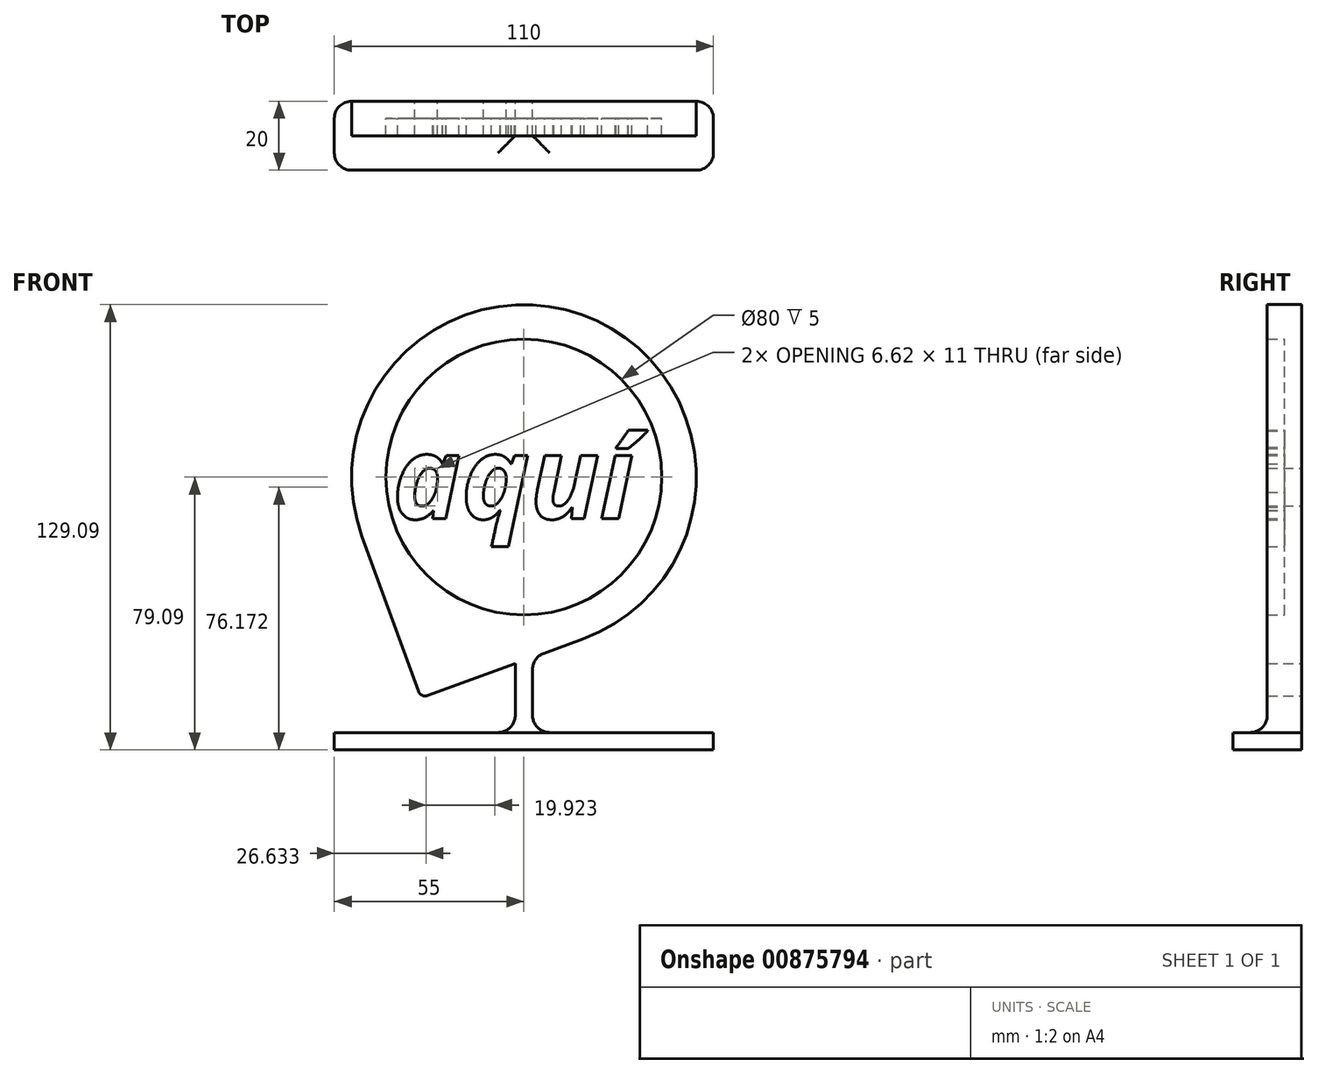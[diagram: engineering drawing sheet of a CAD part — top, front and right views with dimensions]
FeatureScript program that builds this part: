
annotation { "Feature Type Name" : "Feature", "Feature Type Description" : "" }
export const myFeature = defineFeature(function(context is Context, id is Id, definition is map)
    precondition{}
    {
        {
            var Q0;
            Q0=qCreatedBy(makeId("Front.planeOp"),FACE);
            var sketch = newSketch(context, id + "F0", { "sketchPlane" : qUnion([Q0])});
            skCircle(sketch, "E0", {"center": v(0, 0) * mm, "radius": 40 * mm});
            skText(sketch, "E1", { "text": "aquí", "fontName": "OpenSans-BoldItalic.ttf"});
            skArc(sketch, "E2", {"start": v(17.1, -46.98) * mm, "mid": v(21.13, 45.32) * mm, "end": v(-46.98, -17.1) * mm});
            skLineSegment(sketch, "E3", {"start": v(-46.98, -17.1) * mm, "end": v(-29.88, -64.09) * mm});
            skLineSegment(sketch, "E4", {"start": v(-29.88, -64.09) * mm, "end": v(17.1, -46.98) * mm});
            skLineSegment(sketch, "E5", {"start": v(0, 0) * mm, "end": v(0, -76.59) * mm, "construction": true});
            skLineSegment(sketch, "E6.bottom", {"start": v(55, -74.09) * mm, "end": v(-55, -74.09) * mm});
            skLineSegment(sketch, "E6.top", {"start": v(55, -79.09) * mm, "end": v(-55, -79.09) * mm});
            skLineSegment(sketch, "E6.left", {"start": v(55, -74.09) * mm, "end": v(55, -79.09) * mm});
            skLineSegment(sketch, "E6.right", {"start": v(-55, -74.09) * mm, "end": v(-55, -79.09) * mm});
            skPoint(sketch, "E6.middle", {"position": v(0, -76.59) * mm});
            skLineSegment(sketch, "E7.bottom", {"start": v(2.5, -52.3) * mm, "end": v(-2.5, -52.3) * mm});
            skLineSegment(sketch, "E7.top", {"start": v(2.5, -100.87) * mm, "end": v(-2.5, -100.87) * mm});
            skLineSegment(sketch, "E7.left", {"start": v(2.5, -52.3) * mm, "end": v(2.5, -100.87) * mm});
            skLineSegment(sketch, "E7.right", {"start": v(-2.5, -52.3) * mm, "end": v(-2.5, -100.87) * mm});
            const initialGuessF0  = {"E1": [-0.03814, -0.01207, 1, 0, 0.02414]};
            skSetInitialGuess(sketch, initialGuessF0);
            skSolve(sketch);
        }
        {
            var Q0;
            Q0=makeQuery(id+"F0.imprint","IMPRINT",FACE,{"disambiguationData":[TD([[makeQuery(id+"F0.imprint","IMPRINT",EDGE,{"derivedFrom":sQuery(id+"F0.wireOp",EDGE,"E1.sketch_text.stroke-0")}),-1.0]])]});
            var Q1;
            Q1=makeQuery(id+"F0.imprint","IMPRINT",FACE,{"disambiguationData":[TD([[makeQuery(id+"F0.imprint","IMPRINT",EDGE,{"derivedFrom":sQuery(id+"F0.wireOp",EDGE,"E1.sketch_text.stroke-25")}),-1.0]])]});
            var Q2;
            Q2=makeQuery(id+"F0.imprint","IMPRINT",FACE,{"disambiguationData":[TD([[makeQuery(id+"F0.imprint","IMPRINT",EDGE,{"derivedFrom":sQuery(id+"F0.wireOp",EDGE,"E1.sketch_text.stroke-53")}),-1.0]])]});
            var Q3;
            Q3=makeQuery(id+"F0.imprint","IMPRINT",FACE,{"disambiguationData":[TD([[makeQuery(id+"F0.imprint","IMPRINT",EDGE,{"derivedFrom":sQuery(id+"F0.wireOp",EDGE,"E1.sketch_text.stroke-70")}),-1.0]])]});
            var Q4;
            Q4=makeQuery(id+"F0.imprint","IMPRINT",FACE,{"disambiguationData":[TD([[makeQuery(id+"F0.imprint","IMPRINT",EDGE,{"derivedFrom":sQuery(id+"F0.wireOp",EDGE,"E1.sketch_text.stroke-74")}),-1.0]])]});
            var Q5;
            Q5=makeQuery(id+"F0.imprint","IMPRINT",FACE,{"disambiguationData":[TD([[makeQuery(id+"F0.imprint","IMPRINT",EDGE,{"derivedFrom":sQuery(id+"F0.wireOp",EDGE,"E0")}),-1.0]])]});
            extrude(context, id + "F1", {"entities" : qUnion([Q0, Q1, Q2, Q3, Q4, Q5]), "depth" : 10 * mm, "offsetDistance" : 25 * mm});
        }
        {
            var Q0;
            Q0=makeQuery(id+"F0.imprint","IMPRINT",FACE,{"disambiguationData":[TD([[makeQuery(id+"F0.imprint","IMPRINT",EDGE,{"derivedFrom":sQuery(id+"F0.wireOp",EDGE,"E0")}),1.0]])]});
            extrude(context, id + "F2", {"entities" : qUnion([Q0]), "operationType" : NewBodyOperationType.ADD, "depth" : 5 * mm, "offsetDistance" : 25 * mm});
        }
        {
            var Q0;
            Q0=makeQuery(id+"F1.opExtrude","SWEPT_EDGE",EDGE,{"disambiguationData":[OSD([sQuery(id+"F0.wireOp",EDGE,"E3"),sQuery(id+"F0.wireOp",EDGE,"E4")])]});
            fillet(context, id + "F3", {"entities" : qUnion([Q0]), "radius" : 2 * mm, "tangentPropagation" : true, "allowEdgeOverflow" : false});
        }
        {
            var Q0;
            {var subQ0=sQuery(id+"F0.wireOp",EDGE,"E6.right");Q0=makeQuery(id+"F0.imprint","IMPRINT",FACE,{"disambiguationData":[TD([[makeQuery(id+"F0.imprint","IMPRINT",EDGE,{"derivedFrom":subQ0}),1.0]])]});}
            var Q1;
            {var subQ0=sQuery(id+"F0.wireOp",EDGE,"E7.left");var subQ1=sQuery(id+"F0.wireOp",EDGE,"E6.bottom");var subQ2=makeQuery(id+"F0.imprint","INTERSECT",VERTEX,{"derivedFrom":[subQ1,subQ0]});Q1=makeQuery(id+"F0.imprint","IMPRINT",FACE,{"disambiguationData":[TD([[makeQuery(id+"F0.imprint","IMPRINT",EDGE,{"disambiguationData":[TD([[subQ2,-1.0]])],"derivedFrom":subQ1}),1.0]])]});}
            var Q2;
            {var subQ0=sQuery(id+"F0.wireOp",EDGE,"E7.left");var subQ5=sQuery(id+"F0.wireOp",EDGE,"E6.bottom");var subQ6=makeQuery(id+"F0.imprint","INTERSECT",VERTEX,{"derivedFrom":[subQ5,subQ0]});Q2=makeQuery(id+"F0.imprint","IMPRINT",FACE,{"disambiguationData":[TD([[makeQuery(id+"F0.imprint","IMPRINT",EDGE,{"disambiguationData":[TD([[subQ6,-1.0]])],"derivedFrom":subQ5}),-1.0]])]});}
            var Q3;
            {var subQ0=sQuery(id+"F0.wireOp",EDGE,"E7.bottom");Q3=makeQuery(id+"F0.imprint","IMPRINT",FACE,{"disambiguationData":[TD([[makeQuery(id+"F0.imprint","IMPRINT",EDGE,{"derivedFrom":subQ0}),1.0]])]});}
            var Q4;
            {var subQ0=sQuery(id+"F0.wireOp",EDGE,"E6.left");Q4=makeQuery(id+"F0.imprint","IMPRINT",FACE,{"disambiguationData":[TD([[makeQuery(id+"F0.imprint","IMPRINT",EDGE,{"derivedFrom":subQ0}),-1.0]])]});}
            extrude(context, id + "F4", {"entities" : qUnion([Q0, Q1, Q2, Q3, Q4]), "operationType" : NewBodyOperationType.ADD, "depth" : 10 * mm, "offsetDistance" : 25 * mm});
        }
        {
            var Q0;
            {var subQ0=sQuery(id+"F0.wireOp",EDGE,"E6.right");Q0=makeQuery(id+"F0.imprint","IMPRINT",FACE,{"disambiguationData":[TD([[makeQuery(id+"F0.imprint","IMPRINT",EDGE,{"derivedFrom":subQ0}),1.0]])]});}
            var Q1;
            {var subQ0=sQuery(id+"F0.wireOp",EDGE,"E7.left");var subQ1=sQuery(id+"F0.wireOp",EDGE,"E6.bottom");var subQ2=makeQuery(id+"F0.imprint","INTERSECT",VERTEX,{"derivedFrom":[subQ1,subQ0]});Q1=makeQuery(id+"F0.imprint","IMPRINT",FACE,{"disambiguationData":[TD([[makeQuery(id+"F0.imprint","IMPRINT",EDGE,{"disambiguationData":[TD([[subQ2,-1.0]])],"derivedFrom":subQ1}),1.0]])]});}
            var Q2;
            {var subQ0=sQuery(id+"F0.wireOp",EDGE,"E6.left");Q2=makeQuery(id+"F0.imprint","IMPRINT",FACE,{"disambiguationData":[TD([[makeQuery(id+"F0.imprint","IMPRINT",EDGE,{"derivedFrom":subQ0}),-1.0]])]});}
            extrude(context, id + "F5", {"entities" : qUnion([Q0, Q1, Q2]), "operationType" : NewBodyOperationType.ADD, "depth" : 20 * mm, "offsetDistance" : 25 * mm});
        }
        {
            var Q0;
            Q0=makeQuery(id+"F5.opExtrude","CAP_EDGE",EDGE,{"disambiguationData":[OSD([sQuery(id+"F0.wireOp",EDGE,"E6.left")])],"isStart":false});
            var Q1;
            Q1=makeQuery(id+"F5.opExtrude","CAP_EDGE",EDGE,{"disambiguationData":[OSD([sQuery(id+"F0.wireOp",EDGE,"E6.right")])],"isStart":false});
            var Q2;
            Q2=makeQuery(id+"F4.opExtrude","CAP_EDGE",EDGE,{"disambiguationData":[OSD([sQuery(id+"F0.wireOp",EDGE,"E6.right")])],"isStart":true});
            var Q3;
            Q3=makeQuery(id+"F4.opExtrude","CAP_EDGE",EDGE,{"disambiguationData":[OSD([sQuery(id+"F0.wireOp",EDGE,"E6.left")])],"isStart":true});
            fillet(context, id + "F6", {"entities" : qUnion([Q0, Q1, Q2, Q3]), "radius" : 5 * mm, "tangentPropagation" : true, "allowEdgeOverflow" : false});
        }
        {
            var Q0;
            Q0=makeQuery(id+"F4.opExtrude","SWEPT_EDGE",EDGE,{"disambiguationData":[OSD([sQuery(id+"F0.wireOp",EDGE,"E6.bottom"),sQuery(id+"F0.wireOp",EDGE,"E7.left")])]});
            var Q1;
            {var subQ0=sQuery(id+"F0.wireOp",EDGE,"E6.bottom");var subQ1=sQuery(id+"F0.wireOp",EDGE,"E7.right");var subQ2=sQuery(id+"F0.wireOp",EDGE,"E7.bottom");Q1=makeQuery(id+"F5.boolean.opBoolean","INTERSECT",EDGE,{"derivedFrom":[makeQuery(id+"F4.boolean.opBoolean","MERGE",FACE,{"derivedFrom":[makeQuery(id+"F1.opExtrude","CAP_FACE",FACE,{"disambiguationData":[OSD([sQuery(id+"F0.wireOp",EDGE,"E0"),sQuery(id+"F0.wireOp",EDGE,"E2"),sQuery(id+"F0.wireOp",EDGE,"E3"),sQuery(id+"F0.wireOp",EDGE,"E4"),subQ2,subQ1])],"isStart":false}),makeQuery(id+"F4.opExtrude","CAP_FACE",FACE,{"disambiguationData":[OSD([subQ0,sQuery(id+"F0.wireOp",EDGE,"E6.top"),sQuery(id+"F0.wireOp",EDGE,"E6.left"),sQuery(id+"F0.wireOp",EDGE,"E6.right"),subQ2,sQuery(id+"F0.wireOp",EDGE,"E7.left"),subQ1])],"isStart":false})]}),makeQuery(id+"F5.opExtrude","SWEPT_FACE",FACE,{"disambiguationData":[OSD([subQ0])]})]});}
            var Q2;
            Q2=makeQuery(id+"F4.opExtrude","SWEPT_EDGE",EDGE,{"disambiguationData":[OSD([sQuery(id+"F0.wireOp",EDGE,"E6.bottom"),sQuery(id+"F0.wireOp",EDGE,"E7.right")])]});
            var Q3;
            {var subQ0=sQuery(id+"F0.wireOp",EDGE,"E7.left");var subQ1=sQuery(id+"F0.wireOp",EDGE,"E7.bottom");var subQ2=sQuery(id+"F0.wireOp",EDGE,"E4");Q3=makeQuery(id+"F4.boolean.opBoolean","MERGE",EDGE,{"derivedFrom":[makeQuery(id+"F1.opExtrude","SWEPT_EDGE",EDGE,{"disambiguationData":[OSD([subQ2,subQ1,subQ0])]}),makeQuery(id+"F4.opExtrude","SWEPT_EDGE",EDGE,{"disambiguationData":[OSD([subQ2,subQ1,subQ0])]})]});}
            var Q4;
            Q4=makeQuery(id+"F1.opExtrude","SWEPT_EDGE",EDGE,{"disambiguationData":[OSD([sQuery(id+"F0.wireOp",EDGE,"E4"),sQuery(id+"F0.wireOp",EDGE,"E7.right")])]});
            fillet(context, id + "F7", {"entities" : qUnion([Q0, Q1, Q2, Q3, Q4]), "radius" : 5 * mm, "tangentPropagation" : true, "allowEdgeOverflow" : false});
        }
    });
